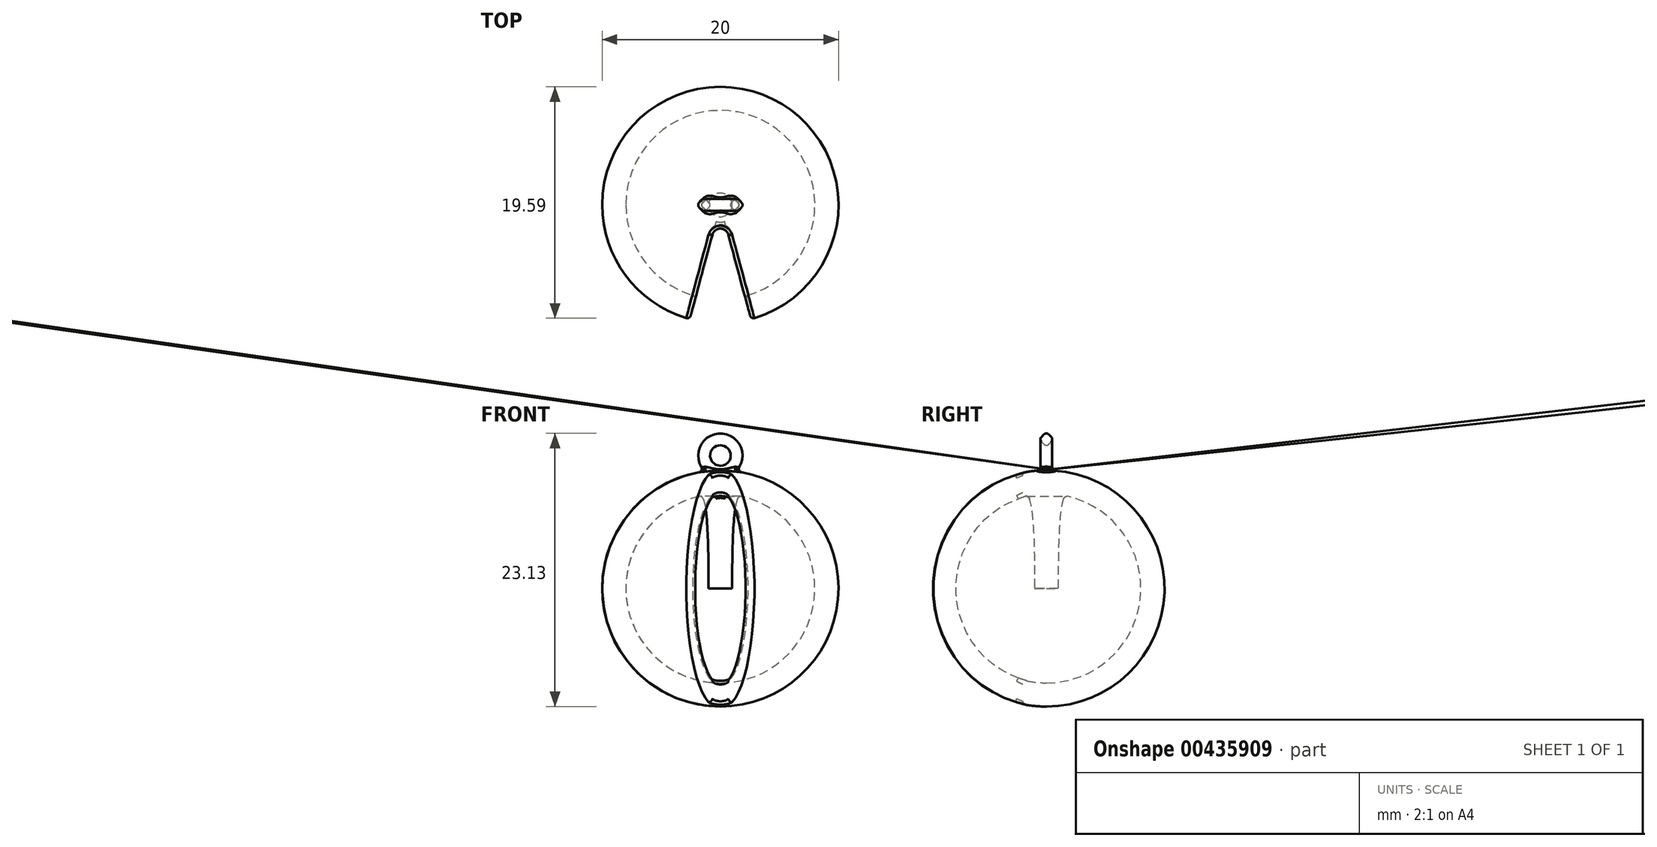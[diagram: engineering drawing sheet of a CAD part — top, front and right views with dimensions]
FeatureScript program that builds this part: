
annotation { "Feature Type Name" : "Feature", "Feature Type Description" : "" }
export const myFeature = defineFeature(function(context is Context, id is Id, definition is map)
    precondition{}
    {
        {
            var Q0;
            Q0=qCreatedBy(makeId("Front.planeOp"),FACE);
            var sketch = newSketch(context, id + "F0", { "sketchPlane" : qUnion([Q0])});
            skLineSegment(sketch, "E0", {"start": v(0, 0) * mm, "end": v(0, -20) * mm});
            skArc(sketch, "E1", {"start": v(0, 0) * mm, "mid": v(10, -10) * mm, "end": v(0, -20) * mm});
            skSolve(sketch);
        }
        {
            var Q0;
            Q0 = qSketchRegion(id + "F0", true);
            var Q1;
            Q1=sQuery(id+"F0.wireOp",EDGE,"E0");
            revolve(context, id + "F1", {"entities" : qUnion([Q0]), "axis" : qUnion([Q1]), "revolveType" : RevolveType.FULL});
        }
        {
            var Q0;
            Q0=qCreatedBy(makeId("Top.planeOp"),FACE);
            var sketch = newSketch(context, id + "F2", { "sketchPlane" : qUnion([Q0])});
            skArc(sketch, "E2", {"start": v(-0.52, -1.93) * mm, "mid": v(0, -2) * mm, "end": v(0.52, -1.93) * mm});
            skLineSegment(sketch, "E3", {"start": v(0, 0) * mm, "end": v(0, -10) * mm, "construction": true});
            skCircle(sketch, "E4", {"center": v(0, 0) * mm, "radius": 10 * mm, "construction": true});
            skLineSegment(sketch, "E5", {"start": v(-0.52, -1.93) * mm, "end": v(-2.59, -9.66) * mm});
            skLineSegment(sketch, "E6", {"start": v(0.52, -1.93) * mm, "end": v(2.59, -9.66) * mm});
            skArc(sketch, "E7", {"start": v(-2.59, -9.66) * mm, "mid": v(0, -10) * mm, "end": v(2.59, -9.66) * mm});
            skSolve(sketch);
        }
        {
            var Q0;
            Q0 = qSketchRegion(id + "F2", true);
            extrude(context, id + "F3", {"entities" : qUnion([Q0]), "operationType" : NewBodyOperationType.REMOVE, "endBound" : BoundingType.THROUGH_ALL, "oppositeDirection" : true, "depth" : 25 * mm, "offsetDistance" : 25 * mm});
        }
        {
            var Q0;
            Q0=qCreatedBy(makeId("Front.planeOp"),FACE);
            var sketch = newSketch(context, id + "F4", { "sketchPlane" : qUnion([Q0])});
            skLineSegment(sketch, "E8", {"start": v(0, 0) * mm, "end": v(0, -20) * mm, "construction": true});
            skSolve(sketch);
        }
        {
            var Q0;
            Q0=qCreatedBy(makeId("Front.planeOp"),FACE);
            var sketch = newSketch(context, id + "F5", { "sketchPlane" : qUnion([Q0])});
            skLineSegment(sketch, "E9", {"start": v(0, -2) * mm, "end": v(0, -18) * mm});
            skArc(sketch, "E10", {"start": v(0, -2) * mm, "mid": v(8, -10) * mm, "end": v(0, -18) * mm});
            skSolve(sketch);
        }
        {
            var Q0;
            Q0 = qSketchRegion(id + "F5", true);
            var Q1;
            Q1=sQuery(id+"F4.wireOp",EDGE,"E8");
            revolve(context, id + "F6", {"operationType" : NewBodyOperationType.REMOVE, "entities" : qUnion([Q0]), "axis" : qUnion([Q1]), "revolveType" : RevolveType.FULL, "oppositeDirection" : true});
        }
        {
            var Q0;
            Q0=makeQuery(id+"F6.boolean.opBoolean","SPLIT",EDGE,{"disambiguationData":[OD(1.0)],"derivedFrom":makeQuery(id+"FYylRN5AXeci3G9_1.1.F3.boolean.opBoolean","COPY",EDGE,{"derivedFrom":makeQuery(id+"FYylRN5AXeci3G9_1.1.F3.opExtrude","SWEPT_EDGE",EDGE,{"disambiguationData":[OSD([sQuery(id+"F2.wireOp",EDGE,"E2"),sQuery(id+"F2.wireOp",EDGE,"E5")])]})})});
            var Q1;
            Q1=makeQuery(id+"F6.boolean.opBoolean","SPLIT",EDGE,{"disambiguationData":[OD(1.0)],"derivedFrom":makeQuery(id+"FYylRN5AXeci3G9_1.1.F3.boolean.opBoolean","COPY",EDGE,{"derivedFrom":makeQuery(id+"FYylRN5AXeci3G9_1.1.F3.opExtrude","SWEPT_EDGE",EDGE,{"disambiguationData":[OSD([sQuery(id+"F2.wireOp",EDGE,"E2"),sQuery(id+"F2.wireOp",EDGE,"E6")])]})})});
            var Q2;
            Q2=makeQuery(id+"F6.boolean.opBoolean","SPLIT",EDGE,{"disambiguationData":[OD(1.0)],"derivedFrom":makeQuery(id+"F3.boolean.opBoolean","COPY",EDGE,{"derivedFrom":makeQuery(id+"F3.opExtrude","SWEPT_EDGE",EDGE,{"disambiguationData":[OSD([sQuery(id+"F2.wireOp",EDGE,"E2"),sQuery(id+"F2.wireOp",EDGE,"E5")])]})})});
            var Q3;
            Q3=makeQuery(id+"F6.boolean.opBoolean","SPLIT",EDGE,{"disambiguationData":[OD(1.0)],"derivedFrom":makeQuery(id+"F3.boolean.opBoolean","COPY",EDGE,{"derivedFrom":makeQuery(id+"F3.opExtrude","SWEPT_EDGE",EDGE,{"disambiguationData":[OSD([sQuery(id+"F2.wireOp",EDGE,"E2"),sQuery(id+"F2.wireOp",EDGE,"E6")])]})})});
            var Q4;
            Q4=makeQuery(id+"F6.boolean.opBoolean","SPLIT",EDGE,{"disambiguationData":[OD(1.0)],"derivedFrom":makeQuery(id+"FYylRN5AXeci3G9_1.7.F3.boolean.opBoolean","COPY",EDGE,{"derivedFrom":makeQuery(id+"FYylRN5AXeci3G9_1.7.F3.opExtrude","SWEPT_EDGE",EDGE,{"disambiguationData":[OSD([sQuery(id+"F2.wireOp",EDGE,"E2"),sQuery(id+"F2.wireOp",EDGE,"E5")])]})})});
            var Q5;
            Q5=makeQuery(id+"F6.boolean.opBoolean","SPLIT",EDGE,{"disambiguationData":[OD(1.0)],"derivedFrom":makeQuery(id+"FYylRN5AXeci3G9_1.7.F3.boolean.opBoolean","COPY",EDGE,{"derivedFrom":makeQuery(id+"FYylRN5AXeci3G9_1.7.F3.opExtrude","SWEPT_EDGE",EDGE,{"disambiguationData":[OSD([sQuery(id+"F2.wireOp",EDGE,"E2"),sQuery(id+"F2.wireOp",EDGE,"E6")])]})})});
            var Q6;
            Q6=makeQuery(id+"F6.boolean.opBoolean","SPLIT",EDGE,{"disambiguationData":[OD(1.0)],"derivedFrom":makeQuery(id+"FYylRN5AXeci3G9_1.6.F3.boolean.opBoolean","COPY",EDGE,{"derivedFrom":makeQuery(id+"FYylRN5AXeci3G9_1.6.F3.opExtrude","SWEPT_EDGE",EDGE,{"disambiguationData":[OSD([sQuery(id+"F2.wireOp",EDGE,"E2"),sQuery(id+"F2.wireOp",EDGE,"E5")])]})})});
            var Q7;
            Q7=makeQuery(id+"F6.boolean.opBoolean","SPLIT",EDGE,{"disambiguationData":[OD(1.0)],"derivedFrom":makeQuery(id+"FYylRN5AXeci3G9_1.5.F3.boolean.opBoolean","COPY",EDGE,{"derivedFrom":makeQuery(id+"FYylRN5AXeci3G9_1.5.F3.opExtrude","SWEPT_EDGE",EDGE,{"disambiguationData":[OSD([sQuery(id+"F2.wireOp",EDGE,"E2"),sQuery(id+"F2.wireOp",EDGE,"E5")])]})})});
            var Q8;
            Q8=makeQuery(id+"F6.boolean.opBoolean","SPLIT",EDGE,{"disambiguationData":[OD(1.0)],"derivedFrom":makeQuery(id+"FYylRN5AXeci3G9_1.5.F3.boolean.opBoolean","COPY",EDGE,{"derivedFrom":makeQuery(id+"FYylRN5AXeci3G9_1.5.F3.opExtrude","SWEPT_EDGE",EDGE,{"disambiguationData":[OSD([sQuery(id+"F2.wireOp",EDGE,"E2"),sQuery(id+"F2.wireOp",EDGE,"E6")])]})})});
            var Q9;
            Q9=makeQuery(id+"F6.boolean.opBoolean","SPLIT",EDGE,{"disambiguationData":[OD(1.0)],"derivedFrom":makeQuery(id+"FYylRN5AXeci3G9_1.4.F3.boolean.opBoolean","COPY",EDGE,{"derivedFrom":makeQuery(id+"FYylRN5AXeci3G9_1.4.F3.opExtrude","SWEPT_EDGE",EDGE,{"disambiguationData":[OSD([sQuery(id+"F2.wireOp",EDGE,"E2"),sQuery(id+"F2.wireOp",EDGE,"E5")])]})})});
            var Q10;
            Q10=makeQuery(id+"F6.boolean.opBoolean","SPLIT",EDGE,{"disambiguationData":[OD(1.0)],"derivedFrom":makeQuery(id+"FYylRN5AXeci3G9_1.4.F3.boolean.opBoolean","COPY",EDGE,{"derivedFrom":makeQuery(id+"FYylRN5AXeci3G9_1.4.F3.opExtrude","SWEPT_EDGE",EDGE,{"disambiguationData":[OSD([sQuery(id+"F2.wireOp",EDGE,"E2"),sQuery(id+"F2.wireOp",EDGE,"E6")])]})})});
            var Q11;
            Q11=makeQuery(id+"F6.boolean.opBoolean","SPLIT",EDGE,{"disambiguationData":[OD(1.0)],"derivedFrom":makeQuery(id+"FYylRN5AXeci3G9_1.3.F3.boolean.opBoolean","COPY",EDGE,{"derivedFrom":makeQuery(id+"FYylRN5AXeci3G9_1.3.F3.opExtrude","SWEPT_EDGE",EDGE,{"disambiguationData":[OSD([sQuery(id+"F2.wireOp",EDGE,"E2"),sQuery(id+"F2.wireOp",EDGE,"E5")])]})})});
            var Q12;
            Q12=makeQuery(id+"F6.boolean.opBoolean","SPLIT",EDGE,{"disambiguationData":[OD(1.0)],"derivedFrom":makeQuery(id+"FYylRN5AXeci3G9_1.3.F3.boolean.opBoolean","COPY",EDGE,{"derivedFrom":makeQuery(id+"FYylRN5AXeci3G9_1.3.F3.opExtrude","SWEPT_EDGE",EDGE,{"disambiguationData":[OSD([sQuery(id+"F2.wireOp",EDGE,"E2"),sQuery(id+"F2.wireOp",EDGE,"E6")])]})})});
            var Q13;
            Q13=makeQuery(id+"F6.boolean.opBoolean","SPLIT",EDGE,{"disambiguationData":[OD(1.0)],"derivedFrom":makeQuery(id+"FYylRN5AXeci3G9_1.2.F3.boolean.opBoolean","COPY",EDGE,{"derivedFrom":makeQuery(id+"FYylRN5AXeci3G9_1.2.F3.opExtrude","SWEPT_EDGE",EDGE,{"disambiguationData":[OSD([sQuery(id+"F2.wireOp",EDGE,"E2"),sQuery(id+"F2.wireOp",EDGE,"E5")])]})})});
            var Q14;
            Q14=makeQuery(id+"F6.boolean.opBoolean","SPLIT",EDGE,{"disambiguationData":[OD(1.0)],"derivedFrom":makeQuery(id+"FYylRN5AXeci3G9_1.2.F3.boolean.opBoolean","COPY",EDGE,{"derivedFrom":makeQuery(id+"FYylRN5AXeci3G9_1.2.F3.opExtrude","SWEPT_EDGE",EDGE,{"disambiguationData":[OSD([sQuery(id+"F2.wireOp",EDGE,"E2"),sQuery(id+"F2.wireOp",EDGE,"E6")])]})})});
            var Q15;
            Q15=makeQuery(id+"F6.boolean.opBoolean","SPLIT",EDGE,{"disambiguationData":[OD(0.0)],"derivedFrom":makeQuery(id+"FYylRN5AXeci3G9_1.5.F3.boolean.opBoolean","COPY",EDGE,{"derivedFrom":makeQuery(id+"FYylRN5AXeci3G9_1.5.F3.opExtrude","SWEPT_EDGE",EDGE,{"disambiguationData":[OSD([sQuery(id+"F2.wireOp",EDGE,"E2"),sQuery(id+"F2.wireOp",EDGE,"E5")])]})})});
            var Q16;
            Q16=makeQuery(id+"F6.boolean.opBoolean","SPLIT",EDGE,{"disambiguationData":[OD(0.0)],"derivedFrom":makeQuery(id+"FYylRN5AXeci3G9_1.4.F3.boolean.opBoolean","COPY",EDGE,{"derivedFrom":makeQuery(id+"FYylRN5AXeci3G9_1.4.F3.opExtrude","SWEPT_EDGE",EDGE,{"disambiguationData":[OSD([sQuery(id+"F2.wireOp",EDGE,"E2"),sQuery(id+"F2.wireOp",EDGE,"E5")])]})})});
            var Q17;
            Q17=makeQuery(id+"F6.boolean.opBoolean","SPLIT",EDGE,{"disambiguationData":[OD(0.0)],"derivedFrom":makeQuery(id+"FYylRN5AXeci3G9_1.4.F3.boolean.opBoolean","COPY",EDGE,{"derivedFrom":makeQuery(id+"FYylRN5AXeci3G9_1.4.F3.opExtrude","SWEPT_EDGE",EDGE,{"disambiguationData":[OSD([sQuery(id+"F2.wireOp",EDGE,"E2"),sQuery(id+"F2.wireOp",EDGE,"E6")])]})})});
            var Q18;
            Q18=makeQuery(id+"F6.boolean.opBoolean","SPLIT",EDGE,{"disambiguationData":[OD(0.0)],"derivedFrom":makeQuery(id+"FYylRN5AXeci3G9_1.3.F3.boolean.opBoolean","COPY",EDGE,{"derivedFrom":makeQuery(id+"FYylRN5AXeci3G9_1.3.F3.opExtrude","SWEPT_EDGE",EDGE,{"disambiguationData":[OSD([sQuery(id+"F2.wireOp",EDGE,"E2"),sQuery(id+"F2.wireOp",EDGE,"E5")])]})})});
            var Q19;
            Q19=makeQuery(id+"F6.boolean.opBoolean","SPLIT",EDGE,{"disambiguationData":[OD(0.0)],"derivedFrom":makeQuery(id+"FYylRN5AXeci3G9_1.3.F3.boolean.opBoolean","COPY",EDGE,{"derivedFrom":makeQuery(id+"FYylRN5AXeci3G9_1.3.F3.opExtrude","SWEPT_EDGE",EDGE,{"disambiguationData":[OSD([sQuery(id+"F2.wireOp",EDGE,"E2"),sQuery(id+"F2.wireOp",EDGE,"E6")])]})})});
            var Q20;
            Q20=makeQuery(id+"F6.boolean.opBoolean","SPLIT",EDGE,{"disambiguationData":[OD(0.0)],"derivedFrom":makeQuery(id+"FYylRN5AXeci3G9_1.2.F3.boolean.opBoolean","COPY",EDGE,{"derivedFrom":makeQuery(id+"FYylRN5AXeci3G9_1.2.F3.opExtrude","SWEPT_EDGE",EDGE,{"disambiguationData":[OSD([sQuery(id+"F2.wireOp",EDGE,"E2"),sQuery(id+"F2.wireOp",EDGE,"E5")])]})})});
            var Q21;
            Q21=makeQuery(id+"F6.boolean.opBoolean","SPLIT",EDGE,{"disambiguationData":[OD(0.0)],"derivedFrom":makeQuery(id+"FYylRN5AXeci3G9_1.2.F3.boolean.opBoolean","COPY",EDGE,{"derivedFrom":makeQuery(id+"FYylRN5AXeci3G9_1.2.F3.opExtrude","SWEPT_EDGE",EDGE,{"disambiguationData":[OSD([sQuery(id+"F2.wireOp",EDGE,"E2"),sQuery(id+"F2.wireOp",EDGE,"E6")])]})})});
            var Q22;
            Q22=makeQuery(id+"F6.boolean.opBoolean","SPLIT",EDGE,{"disambiguationData":[OD(0.0)],"derivedFrom":makeQuery(id+"FYylRN5AXeci3G9_1.1.F3.boolean.opBoolean","COPY",EDGE,{"derivedFrom":makeQuery(id+"FYylRN5AXeci3G9_1.1.F3.opExtrude","SWEPT_EDGE",EDGE,{"disambiguationData":[OSD([sQuery(id+"F2.wireOp",EDGE,"E2"),sQuery(id+"F2.wireOp",EDGE,"E5")])]})})});
            var Q23;
            Q23=makeQuery(id+"F6.boolean.opBoolean","SPLIT",EDGE,{"disambiguationData":[OD(0.0)],"derivedFrom":makeQuery(id+"FYylRN5AXeci3G9_1.1.F3.boolean.opBoolean","COPY",EDGE,{"derivedFrom":makeQuery(id+"FYylRN5AXeci3G9_1.1.F3.opExtrude","SWEPT_EDGE",EDGE,{"disambiguationData":[OSD([sQuery(id+"F2.wireOp",EDGE,"E2"),sQuery(id+"F2.wireOp",EDGE,"E6")])]})})});
            var Q24;
            Q24=makeQuery(id+"F6.boolean.opBoolean","SPLIT",EDGE,{"disambiguationData":[OD(0.0)],"derivedFrom":makeQuery(id+"F3.boolean.opBoolean","COPY",EDGE,{"derivedFrom":makeQuery(id+"F3.opExtrude","SWEPT_EDGE",EDGE,{"disambiguationData":[OSD([sQuery(id+"F2.wireOp",EDGE,"E2"),sQuery(id+"F2.wireOp",EDGE,"E5")])]})})});
            var Q25;
            Q25=makeQuery(id+"F6.boolean.opBoolean","SPLIT",EDGE,{"disambiguationData":[OD(0.0)],"derivedFrom":makeQuery(id+"F3.boolean.opBoolean","COPY",EDGE,{"derivedFrom":makeQuery(id+"F3.opExtrude","SWEPT_EDGE",EDGE,{"disambiguationData":[OSD([sQuery(id+"F2.wireOp",EDGE,"E2"),sQuery(id+"F2.wireOp",EDGE,"E6")])]})})});
            var Q26;
            Q26=makeQuery(id+"F6.boolean.opBoolean","SPLIT",EDGE,{"disambiguationData":[OD(0.0)],"derivedFrom":makeQuery(id+"FYylRN5AXeci3G9_1.7.F3.boolean.opBoolean","COPY",EDGE,{"derivedFrom":makeQuery(id+"FYylRN5AXeci3G9_1.7.F3.opExtrude","SWEPT_EDGE",EDGE,{"disambiguationData":[OSD([sQuery(id+"F2.wireOp",EDGE,"E2"),sQuery(id+"F2.wireOp",EDGE,"E5")])]})})});
            var Q27;
            Q27=makeQuery(id+"F6.boolean.opBoolean","SPLIT",EDGE,{"disambiguationData":[OD(0.0)],"derivedFrom":makeQuery(id+"FYylRN5AXeci3G9_1.7.F3.boolean.opBoolean","COPY",EDGE,{"derivedFrom":makeQuery(id+"FYylRN5AXeci3G9_1.7.F3.opExtrude","SWEPT_EDGE",EDGE,{"disambiguationData":[OSD([sQuery(id+"F2.wireOp",EDGE,"E2"),sQuery(id+"F2.wireOp",EDGE,"E6")])]})})});
            var Q28;
            Q28=makeQuery(id+"F6.boolean.opBoolean","SPLIT",EDGE,{"disambiguationData":[OD(0.0)],"derivedFrom":makeQuery(id+"FYylRN5AXeci3G9_1.6.F3.boolean.opBoolean","COPY",EDGE,{"derivedFrom":makeQuery(id+"FYylRN5AXeci3G9_1.6.F3.opExtrude","SWEPT_EDGE",EDGE,{"disambiguationData":[OSD([sQuery(id+"F2.wireOp",EDGE,"E2"),sQuery(id+"F2.wireOp",EDGE,"E5")])]})})});
            var Q29;
            Q29=makeQuery(id+"F6.boolean.opBoolean","SPLIT",EDGE,{"disambiguationData":[OD(0.0)],"derivedFrom":makeQuery(id+"FYylRN5AXeci3G9_1.6.F3.boolean.opBoolean","COPY",EDGE,{"derivedFrom":makeQuery(id+"FYylRN5AXeci3G9_1.6.F3.opExtrude","SWEPT_EDGE",EDGE,{"disambiguationData":[OSD([sQuery(id+"F2.wireOp",EDGE,"E2"),sQuery(id+"F2.wireOp",EDGE,"E6")])]})})});
            var Q30;
            Q30=makeQuery(id+"F6.boolean.opBoolean","SPLIT",EDGE,{"disambiguationData":[OD(1.0)],"derivedFrom":makeQuery(id+"FYylRN5AXeci3G9_1.6.F3.boolean.opBoolean","COPY",EDGE,{"derivedFrom":makeQuery(id+"FYylRN5AXeci3G9_1.6.F3.opExtrude","SWEPT_EDGE",EDGE,{"disambiguationData":[OSD([sQuery(id+"F2.wireOp",EDGE,"E2"),sQuery(id+"F2.wireOp",EDGE,"E6")])]})})});
            var Q31;
            Q31=makeQuery(id+"F6.boolean.opBoolean","SPLIT",EDGE,{"disambiguationData":[OD(0.0)],"derivedFrom":makeQuery(id+"FYylRN5AXeci3G9_1.5.F3.boolean.opBoolean","COPY",EDGE,{"derivedFrom":makeQuery(id+"FYylRN5AXeci3G9_1.5.F3.opExtrude","SWEPT_EDGE",EDGE,{"disambiguationData":[OSD([sQuery(id+"F2.wireOp",EDGE,"E2"),sQuery(id+"F2.wireOp",EDGE,"E6")])]})})});
            fillet(context, id + "F7", {"entities" : qUnion([Q0, Q1, Q2, Q3, Q4, Q5, Q6, Q7, Q8, Q9, Q10, Q11, Q12, Q13, Q14, Q15, Q16, Q17, Q18, Q19, Q20, Q21, Q22, Q23, Q24, Q25, Q26, Q27, Q28, Q29, Q30, Q31]), "radius" : 0.7 * mm, "tangentPropagation" : true, "allowEdgeOverflow" : false});
        }
        {
            var Q0;
            Q0=makeQuery(id+"F1.opRevolve","SWEPT_FACE",FACE,{"disambiguationData":[OSD([sQuery(id+"F0.wireOp",EDGE,"E1")])]});
            var Q1;
            Q1=makeQuery(id+"F6.boolean.opBoolean","COPY",FACE,{"derivedFrom":makeQuery(id+"F6.opRevolve","SWEPT_FACE",FACE,{"disambiguationData":[OSD([sQuery(id+"F5.wireOp",EDGE,"E10")])]})});
            fillet(context, id + "F8", {"entities" : qUnion([Q0, Q1]), "radius" : 0.3 * mm, "tangentPropagation" : true, "allowEdgeOverflow" : false});
        }
        {
            var Q0;
            Q0=qCreatedBy(makeId("Front.planeOp"),FACE);
            var sketch = newSketch(context, id + "F9", { "sketchPlane" : qUnion([Q0])});
            skCircle(sketch, "E11", {"center": v(0, 1.25) * mm, "radius": 0.75 * mm});
            skCircle(sketch, "E12", {"center": v(0, 1.25) * mm, "radius": 2 * mm});
            skSolve(sketch);
        }
        {
            var Q0;
            Q0 = qSketchRegion(id + "F9", true);
            extrude(context, id + "F10", {"entities" : qUnion([Q0]), "operationType" : NewBodyOperationType.ADD, "depth" : 1 * mm, "offsetDistance" : 25 * mm, "hasDraft" : true, "draftAngle" : 45 * degree, "draftPullDirection" : true, "hasSecondDirection" : true, "secondDirectionOppositeDirection" : true, "secondDirectionDepth" : 1 * mm, "hasSecondDirectionDraft" : true, "secondDirectionDraftAngle" : 45 * degree, "secondDirectionDraftPullDirection" : true});
        }
        {
            var Q0;
            {var subQ0=makeQuery(id+"F10.opExtrude","SWEPT_FACE",FACE,{"disambiguationData":[OSD([sQuery(id+"F9.wireOp",EDGE,"E12")])]});Q0=makeQuery(id+"F10.*.booleanUnion.opBoolean","MERGE",EDGE,{"derivedFrom":[makeQuery(id+"F10.*.split.splitOp","SPLIT_SURFACE_INTERSECT",EDGE,{"derivedFrom":[subQ0]}),makeQuery(id+"F10.*.split.splitOp","SPLIT_SURFACE_INTERSECT",EDGE,{"derivedFrom":[subQ0],"isFromBackBody":true})]});}
            var Q1;
            Q1=makeQuery(id+"F10.*.draftFirst.opDraft","TWEAK_EDGE",EDGE,{"derivedFrom":[makeQuery(id+"F10.*.split.splitOp","SPLIT",FACE,{"derivedFrom":makeQuery(id+"F10.opExtrude","SWEPT_FACE",FACE,{"disambiguationData":[OSD([sQuery(id+"F9.wireOp",EDGE,"E11")])]})}),makeQuery(id+"F10.*.split.splitOp","SPLIT",FACE,{"derivedFrom":makeQuery(id+"F10.opExtrude","SWEPT_FACE",FACE,{"disambiguationData":[OSD([sQuery(id+"F9.wireOp",EDGE,"E12")])]})})]});
            var Q2;
            Q2=makeQuery(id+"F10.*.draftSecond.opDraft","TWEAK_EDGE",EDGE,{"derivedFrom":[makeQuery(id+"F10.*.split.splitOp","SPLIT",FACE,{"derivedFrom":makeQuery(id+"F10.opExtrude","SWEPT_FACE",FACE,{"disambiguationData":[OSD([sQuery(id+"F9.wireOp",EDGE,"E11")])]}),"isFromBackBody":true}),makeQuery(id+"F10.*.split.splitOp","SPLIT",FACE,{"derivedFrom":makeQuery(id+"F10.opExtrude","SWEPT_FACE",FACE,{"disambiguationData":[OSD([sQuery(id+"F9.wireOp",EDGE,"E12")])]}),"isFromBackBody":true})]});
            var Q3;
            {var subQ0=makeQuery(id+"F10.opExtrude","SWEPT_FACE",FACE,{"disambiguationData":[OSD([sQuery(id+"F9.wireOp",EDGE,"E11")])]});Q3=makeQuery(id+"F10.*.booleanUnion.opBoolean","MERGE",EDGE,{"derivedFrom":[makeQuery(id+"F10.*.split.splitOp","SPLIT_SURFACE_INTERSECT",EDGE,{"derivedFrom":[subQ0]}),makeQuery(id+"F10.*.split.splitOp","SPLIT_SURFACE_INTERSECT",EDGE,{"derivedFrom":[subQ0],"isFromBackBody":true})]});}
            fillet(context, id + "F11", {"entities" : qUnion([Q0, Q1, Q2, Q3]), "radius" : 0.3 * mm, "tangentPropagation" : true, "allowEdgeOverflow" : false});
        }
        {
            var Q0;
            Q0=makeQuery(id+"F11.opFillet","BLEND_EDGE",EDGE,{"blendedFrom":[makeQuery(id+"F10.*.draftFirst.opDraft","TWEAK_EDGE",EDGE,{"derivedFrom":[makeQuery(id+"F10.*.split.splitOp","SPLIT",FACE,{"derivedFrom":makeQuery(id+"F10.opExtrude","SWEPT_FACE",FACE,{"disambiguationData":[OSD([sQuery(id+"F9.wireOp",EDGE,"E11")])]})}),makeQuery(id+"F10.*.split.splitOp","SPLIT",FACE,{"derivedFrom":makeQuery(id+"F10.opExtrude","SWEPT_FACE",FACE,{"disambiguationData":[OSD([sQuery(id+"F9.wireOp",EDGE,"E12")])]})})]}),makeQuery(id+"F1.opRevolve","SWEPT_FACE",FACE,{"disambiguationData":[OSD([sQuery(id+"F0.wireOp",EDGE,"E1")])]})],"blendedInto":[makeQuery(id+"F1.opRevolve","SWEPT_FACE",FACE,{"disambiguationData":[OSD([sQuery(id+"F0.wireOp",EDGE,"E1")])]})]});
            fillet(context, id + "F12", {"entities" : qUnion([Q0]), "radius" : 0.3 * mm, "tangentPropagation" : true, "allowEdgeOverflow" : false});
        }
        {
            var Q0;
            Q0=qCreatedBy(makeId("Front.planeOp"),FACE);
            var sketch = newSketch(context, id + "F13", { "sketchPlane" : qUnion([Q0])});
            skLineSegment(sketch, "E13", {"start": v(0, 0) * mm, "end": v(0, -20) * mm, "construction": true});
            skLineSegment(sketch, "E14", {"start": v(0, -10) * mm, "end": v(1, -10) * mm});
            skFitSpline(sketch, "E15", {"points": [v(1.64, -2.17) * mm, v(1, -10) * mm], "startDerivative": vector(-1.92, -0.87) * mm, "endDerivative": vector(0, -7.5) * mm});
            skLineSegment(sketch, "E16", {"start": v(1, -10) * mm, "end": v(1, -4.2) * mm, "construction": true});
            skLineSegment(sketch, "E17", {"start": v(0, -1.44) * mm, "end": v(0, -10) * mm});
            skLineSegment(sketch, "E18", {"start": v(1.64, -2.17) * mm, "end": v(1.64, -1.44) * mm});
            skLineSegment(sketch, "E19", {"start": v(1.64, -1.44) * mm, "end": v(0, -1.44) * mm});
            skLineSegment(sketch, "E20", {"start": v(0, -1.44) * mm, "end": v(0, -1.44) * mm});
            skSolve(sketch);
        }
        {
            var Q0;
            Q0 = qSketchRegion(id + "F13", true);
            var Q1;
            Q1=sQuery(id+"F13.wireOp",EDGE,"E13");
            revolve(context, id + "F14", {"operationType" : NewBodyOperationType.ADD, "entities" : qUnion([Q0]), "axis" : qUnion([Q1]), "revolveType" : RevolveType.FULL});
        }
        {
            var Q0;
            Q0=qCreatedBy(makeId("Top.planeOp"),FACE);
            cPlane(context, id + "F15", {"entities" : qUnion([Q0]), "cplaneType" : CPlaneType.OFFSET, "offset" : 10 * mm, "oppositeDirection" : true, "width" : 150 * mm, "height" : 150 * mm});
        }
        {
            var Q0;
            {var subQ0=sQuery(id+"F5.wireOp",EDGE,"E10");var subQ1=makeQuery(id+"F6.boolean.opBoolean","COPY",FACE,{"derivedFrom":makeQuery(id+"F6.opRevolve","SWEPT_FACE",FACE,{"disambiguationData":[OSD([subQ0])]})});var subQ3=sQuery(id+"F2.wireOp",EDGE,"E2");var subQ4=sQuery(id+"F2.wireOp",EDGE,"E5");var subQ5=sQuery(id+"F13.wireOp",EDGE,"E15");Q0=makeQuery(id+"F14.boolean.opBoolean","SPLIT",EDGE,{"disambiguationData":[TD([makeQuery(id+"F8.opFillet","BLEND_FACE",FACE,{"disambiguationData":[OSD([subQ3,subQ4,subQ0]),TDD([makeQuery(id+"F7.opFillet","BLEND_EDGE",EDGE,{"blendedFrom":[makeQuery(id+"F6.boolean.opBoolean","SPLIT",EDGE,{"disambiguationData":[OD(1.0)],"derivedFrom":makeQuery(id+"FYylRN5AXeci3G9_1.7.F3.boolean.opBoolean","COPY",EDGE,{"derivedFrom":makeQuery(id+"FYylRN5AXeci3G9_1.7.F3.opExtrude","SWEPT_EDGE",EDGE,{"disambiguationData":[OSD([subQ3,subQ4])]})})}),subQ1],"blendedInto":[subQ1]})])]})])],"derivedFrom":makeQuery(id+"F14.opRevolve","SWEPT_EDGE",EDGE,{"disambiguationData":[OSD([subQ5,sQuery(id+"F13.wireOp",EDGE,"E18")])]})});}
            var Q1;
            {var subQ0=sQuery(id+"F5.wireOp",EDGE,"E10");var subQ1=makeQuery(id+"F6.boolean.opBoolean","COPY",FACE,{"derivedFrom":makeQuery(id+"F6.opRevolve","SWEPT_FACE",FACE,{"disambiguationData":[OSD([subQ0])]})});var subQ3=sQuery(id+"F2.wireOp",EDGE,"E2");var subQ4=sQuery(id+"F2.wireOp",EDGE,"E5");var subQ5=sQuery(id+"F13.wireOp",EDGE,"E15");Q1=makeQuery(id+"FLe4KydfltoYJVj_1.1.F14.boolean.opBoolean","SPLIT",EDGE,{"disambiguationData":[TD([makeQuery(id+"F8.opFillet","BLEND_FACE",FACE,{"disambiguationData":[OSD([subQ3,subQ4,subQ0]),TDD([makeQuery(id+"F7.opFillet","BLEND_EDGE",EDGE,{"blendedFrom":[makeQuery(id+"F6.boolean.opBoolean","SPLIT",EDGE,{"disambiguationData":[OD(0.0)],"derivedFrom":makeQuery(id+"FYylRN5AXeci3G9_1.7.F3.boolean.opBoolean","COPY",EDGE,{"derivedFrom":makeQuery(id+"FYylRN5AXeci3G9_1.7.F3.opExtrude","SWEPT_EDGE",EDGE,{"disambiguationData":[OSD([subQ3,subQ4])]})})}),subQ1],"blendedInto":[subQ1]})])]})])],"derivedFrom":makeQuery(id+"FLe4KydfltoYJVj_1.1.F14.opRevolve","SWEPT_EDGE",EDGE,{"disambiguationData":[OSD([subQ5,sQuery(id+"F13.wireOp",EDGE,"E18")])]})});}
            fillet(context, id + "F16", {"entities" : qUnion([Q0, Q1]), "radius" : 0.3 * mm, "tangentPropagation" : true, "allowEdgeOverflow" : false});
        }
    });
